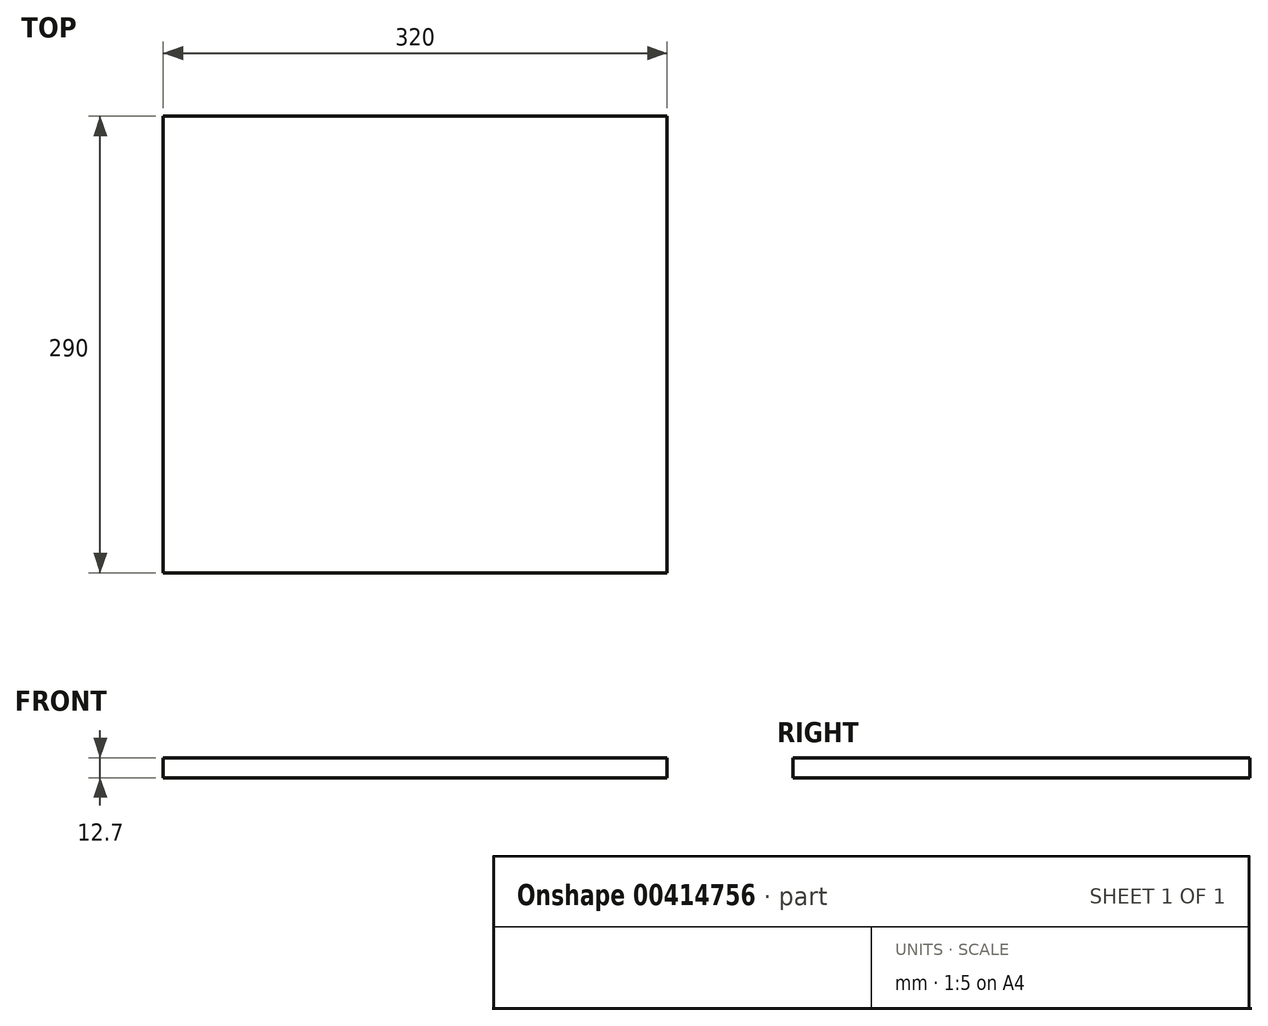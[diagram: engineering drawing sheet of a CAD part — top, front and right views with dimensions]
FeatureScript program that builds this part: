
annotation { "Feature Type Name" : "Feature", "Feature Type Description" : "" }
export const myFeature = defineFeature(function(context is Context, id is Id, definition is map)
    precondition{}
    {
        {
            var Q0;
            Q0=qCreatedBy(makeId("Top.planeOp"),FACE);
            var sketch = newSketch(context, id + "F0", { "sketchPlane" : qUnion([Q0])});
            skLineSegment(sketch, "E0.bottom", {"start": v(-70.96, 65.05) * mm, "end": v(249.04, 65.05) * mm});
            skLineSegment(sketch, "E0.top", {"start": v(-70.96, -224.95) * mm, "end": v(249.04, -224.95) * mm});
            skLineSegment(sketch, "E0.left", {"start": v(-70.96, 65.05) * mm, "end": v(-70.96, -224.95) * mm});
            skLineSegment(sketch, "E0.right", {"start": v(249.04, 65.05) * mm, "end": v(249.04, -224.95) * mm});
            skSolve(sketch);
        }
        {
            var Q0;
            Q0=qSketchRegion(id+"F0",true);
            extrude(context, id + "F1", {"entities" : qUnion([Q0]), "depth" : 12.7 * mm});
        }
    });
